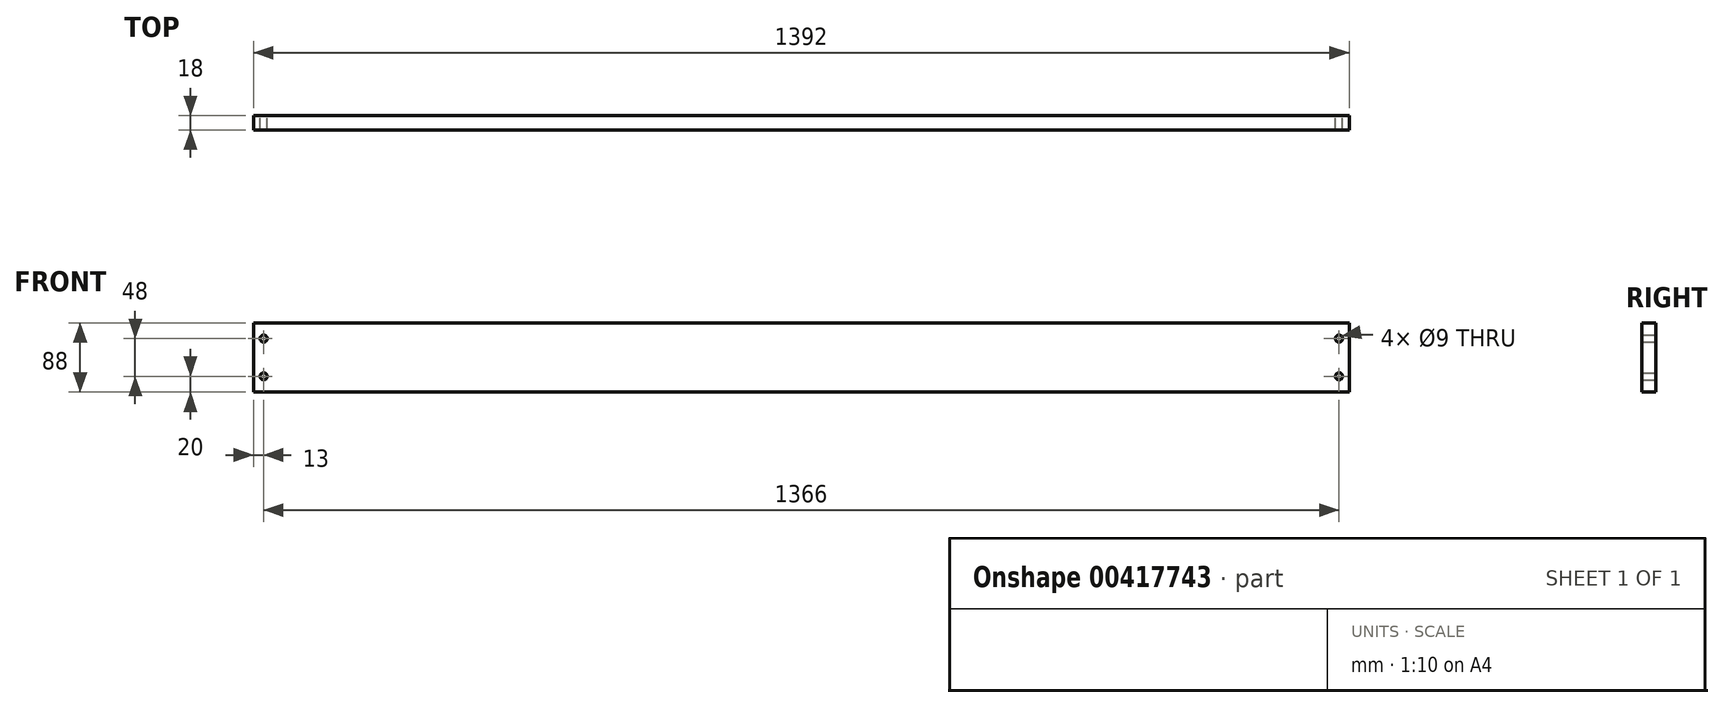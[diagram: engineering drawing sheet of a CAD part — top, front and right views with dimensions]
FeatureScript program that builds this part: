
annotation { "Feature Type Name" : "Feature", "Feature Type Description" : "" }
export const myFeature = defineFeature(function(context is Context, id is Id, definition is map)
    precondition{}
    {
        {
            var Q0;
            Q0=qCreatedBy(makeId("Right.planeOp"),FACE);
            var sketch = newSketch(context, id + "F0", { "sketchPlane" : qUnion([Q0])});
            skLineSegment(sketch, "E0.bottom", {"start": v(0, 44) * mm, "end": v(18, 44) * mm});
            skLineSegment(sketch, "E0.top", {"start": v(0, -44) * mm, "end": v(18, -44) * mm});
            skLineSegment(sketch, "E0.left", {"start": v(0, 44) * mm, "end": v(0, -44) * mm});
            skLineSegment(sketch, "E0.right", {"start": v(18, 44) * mm, "end": v(18, -44) * mm});
            skSolve(sketch);
        }
        {
            var Q0;
            Q0 = qSketchRegion(id + "F0", true);
            extrude(context, id + "F1", {"entities" : qUnion([Q0]), "depth" : 696 * mm});
        }
        {
            var Q0;
            Q0=makeQuery(id+"F1.opExtrude","SWEPT_FACE",FACE,{"disambiguationData":[OSD([sQuery(id+"F0.wireOp",EDGE,"E0.right")])]});
            var sketch = newSketch(context, id + "F2", { "sketchPlane" : qUnion([Q0])});
            skLineSegment(sketch, "E1", {"start": v(-683, 44) * mm, "end": v(-683, -44) * mm, "construction": true});
            skCircle(sketch, "E2", {"center": v(-683, 24) * mm, "radius": 4.5 * mm});
            skCircle(sketch, "E3", {"center": v(-683, -24) * mm, "radius": 4.5 * mm});
            skLineSegment(sketch, "E4", {"start": v(-696, 0) * mm, "end": v(-683, 0) * mm, "construction": true});
            skSolve(sketch);
        }
        {
            var Q0;
            Q0 = qSketchRegion(id + "F2", true);
            extrude(context, id + "F3", {"entities" : qUnion([Q0]), "operationType" : NewBodyOperationType.REMOVE, "endBound" : BoundingType.THROUGH_ALL, "oppositeDirection" : true, "depth" : 25 * mm});
        }
        {
            var Q0;
            Q0=makeQuery(id+"F1.opExtrude","SWEPT_BODY",BODY,{"disambiguationData":[OSD([sQuery(id+"F0.wireOp",EDGE,"E0.bottom"),sQuery(id+"F0.wireOp",EDGE,"E0.top"),sQuery(id+"F0.wireOp",EDGE,"E0.left"),sQuery(id+"F0.wireOp",EDGE,"E0.right")])]});
            var Q1;
            Q1=qCreatedBy(makeId("Right.planeOp"),FACE);
            mirror(context, id + "F4", {"operationType" : NewBodyOperationType.ADD, "entities" : qUnion([Q0]), "mirrorPlane" : qUnion([Q1])});
        }
    });
